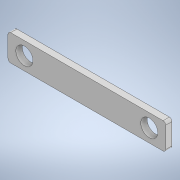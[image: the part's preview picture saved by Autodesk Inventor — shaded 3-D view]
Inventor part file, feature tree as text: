
AUTODESK INVENTOR PART (.ipt)
format: ipt  version: 2021 (Build 250183000, 183)  size: 117,248 bytes
history: native  units: mm
features: extrude x2, sketch x2, fillet x1, projected_geometry x1
ambient origin geometry x8: Origin, YZ Plane, XZ Plane, XY Plane, X Axis, Y Axis, Z Axis, Center Point
bodies: Solid1 (feature_tree)
feature tree (6):
  extrude  "Extrusion1"  Depth=20.0mm
  extrude  "Extrusion2"  Depth=2.0mm
  fillet  "Fillet1"  Radius=13.0mm
  sketch  "Sketch1"  dims[d0=120.0mm d1=20.0mm]
  sketch  "Sketch2"  dims[d2=4.8mm d3=0.0mm d4=13.0mm d5=13.0mm d6=95.0mm d7=0.0mm d8=0.0mm d9=2.0mm]
  projected_geometry  "Projected Loop1"
